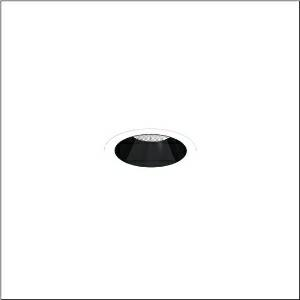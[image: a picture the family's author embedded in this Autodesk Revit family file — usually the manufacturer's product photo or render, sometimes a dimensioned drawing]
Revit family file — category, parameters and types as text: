
# Revit family: lunis_21_m_51db17tc91c
name_source: partatom
category: Lighting Fixtures
units: mm (PartAtom-declared; Revit-internal decimal feet)

## family parameters
Cut with Voids When Loaded = No
Host = Face
Light Source = No
Part Type = Normal
Room Calculation Point = No
Round Connector Dimension = Use Diameter
Shared = No

## types (1)
- --- (1 x LED 3000 K ... 6500 K, 3340 lm, 26 W, 4000K)
    Apparent Load = 26 VA
    CIE Flux Codes = 98 100 100 100 100
    Color Rendering = 80
    Color Temperature = 4000K
    Default Elevation = 1800 mm
    Description = Lunis 21 M, downlight, light control with lens, of PMMA, anti glare with reflector, of aluminium, light emission: direct distribution, LED rated luminous flux: 3.340lm, light colour: 8tw, with terminal, 5-pole, mains connection: 220..240V, AC/DC, 0/50..60Hz, housing, round, of diecast aluminium, traffic white (RAL 9016), diameter: 115mm, clamping range: 1..40mm, protection rating (complete): IP20, protection rating (on room side): IP54, insulation class (complete): insulation class II (safety insulation), certification: CE, impact resistance: IK03, packaging unit: 1 piece
    Height = 0 mm  [stored 0 ft]
    Lamp = 1 x LED 3000 K ... 6500 K
    Lamp Light Flux = 3340 lm
    Lamp Power = 26 W
    Lamp count = 1
    Length = 115 mm
    Luminous efficacy = 128 lm/W
    Manufacturer = Siteco
    ModVariant = No
    Model = 51DB17TC91C
    Mounting Place = Ceiling
    Mounting Type = Recessed
    Number of Poles = 1
    OnlyDefault = Yes
    Power Factor = 1
    Product Name = Lunis 21 M
    Product group = downlight
    ProductGroupID = 401
    Protection Class = Protection class II
    Protection Degree = IP 20
    RLX_Detail_Level = 1
    RLX_Emergency_Light_Flux = 0 lm
    RLX_Emergency_Type = 0
    RLX_Emergency_Type_DB = No
    RlxData = <blob elided: 11417 chars, md5=cf3d7055>
    Socket = socket
    Standby Power = 0 W
    System Light Flux = 3340 lm
    System Power = 26 W
    Type Comments = individual setting: CCT=4000K, colour temperature 4000K, luminous flux: 100 % | (ON | ON | OFF | OFF) | 700 mA
    Type Image = l_1290854.jpg
    URL = http://relux.com
    VarID = @adj_035883
    Voltage = 0 V
    Weight = 0.00 kg
    Width = 0 mm  [stored 0 ft]

note: [stored X ft] marks values corroborated as IEEE doubles in the binary element streams (Revit-internal decimal feet)

## geometry (parser evidence)
native form markers: Sweep x8
no freeform markers — native parametric forms only
